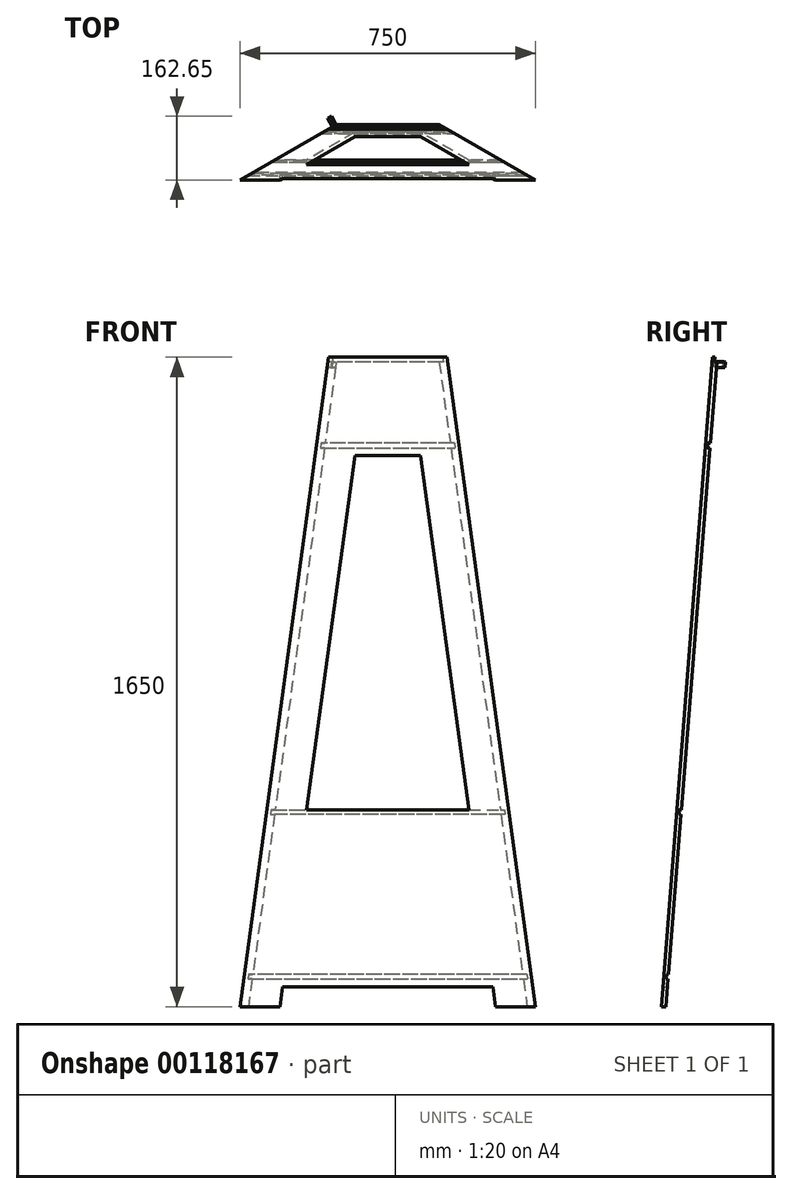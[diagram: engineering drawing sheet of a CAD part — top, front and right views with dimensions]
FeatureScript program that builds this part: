
annotation { "Feature Type Name" : "Feature", "Feature Type Description" : "" }
export const myFeature = defineFeature(function(context is Context, id is Id, definition is map)
    precondition{}
    {
        {
            var Q0;
            Q0=qCreatedBy(makeId("Front.planeOp"),FACE);
            var sketch = newSketch(context, id + "F0", { "sketchPlane" : qUnion([Q0])});
            skLineSegment(sketch, "E0", {"start": v(-375, 0) * mm, "end": v(375, 0) * mm});
            skLineSegment(sketch, "E1", {"start": v(0, 0) * mm, "end": v(0, 1650) * mm});
            skLineSegment(sketch, "E2", {"start": v(-150, 1650) * mm, "end": v(150, 1650) * mm});
            skSolve(sketch);
        }
        {
            var Q0;
            Q0=sQuery(id+"F0.wireOp",EDGE,"E2");
            cPoint(context, id + "F1", {"entities" : qUnion([Q0]), "parameter" : 0.5});
        }
        {
            var Q0;
            Q0 = qCreatedBy(id + "F1" ,VERTEX);
            var Q1;
            Q1=sQuery(id+"F0.wireOp",EDGE,"E1");
            cPlane(context, id + "F2", {"entities" : qUnion([Q0, Q1]), "cplaneType" : CPlaneType.LINE_POINT, "offset" : 25 * mm, "width" : 150 * mm, "height" : 150 * mm});
        }
        {
            var Q0;
            Q0=qCreatedBy(makeId("Top.planeOp"),FACE);
            var sketch = newSketch(context, id + "F3", { "sketchPlane" : qUnion([Q0])});
            skCircle(sketch, "E3.cCircle", {"center": v(0, 0) * mm, "radius": 216.5 * mm, "construction": true});
            skLineSegment(sketch, "E3.0", {"start": v(375, -216.5) * mm, "end": v(-375, -216.5) * mm});
            skLineSegment(sketch, "E3.1", {"start": v(-375, -216.5) * mm, "end": v(0, 433.01) * mm});
            skLineSegment(sketch, "E3.2", {"start": v(0, 433.01) * mm, "end": v(375, -216.5) * mm});
            skPoint(sketch, "E3.0.midPoint", {"position": v(0, -216.5) * mm});
            skSolve(sketch);
        }
        {
            var Q0;
            Q0=qCreatedBy(id+"F2.planeOp",FACE);
            var sketch = newSketch(context, id + "F4", { "sketchPlane" : qUnion([Q0])});
            skCircle(sketch, "E4.cCircle", {"center": v(0, 0) * mm, "radius": 86.6 * mm, "construction": true});
            skLineSegment(sketch, "E4.0", {"start": v(150, -86.6) * mm, "end": v(-150, -86.6) * mm});
            skLineSegment(sketch, "E4.1", {"start": v(-150, -86.6) * mm, "end": v(0, 173.2) * mm});
            skLineSegment(sketch, "E4.2", {"start": v(0, 173.2) * mm, "end": v(150, -86.6) * mm});
            skPoint(sketch, "E4.0.midPoint", {"position": v(0, -86.6) * mm});
            skSolve(sketch);
        }
        {
            var Q0;
            Q0=makeQuery(id+"F3.imprint","IMPRINT",FACE,{"disambiguationData":[TD([[makeQuery(id+"F3.imprint","IMPRINT",EDGE,{"derivedFrom":sQuery(id+"F3.wireOp",EDGE,"E3.0")}),-1.0]])]});
            var Q1;
            Q1=makeQuery(id+"F4.imprint","IMPRINT",FACE,{"disambiguationData":[TD([[makeQuery(id+"F4.imprint","IMPRINT",EDGE,{"derivedFrom":sQuery(id+"F4.wireOp",EDGE,"E4.0")}),-1.0]])]});
            loft(context, id + "F5", {"sheetProfilesArray" : [{ "sheetProfileEntities" : qUnion([Q0]) }, { "sheetProfileEntities" : qUnion([Q1]) }]});
        }
        {
            var Q0;
            {var subQ0=sQuery(id+"F4.wireOp",EDGE,"E4.0");var subQ1=sQuery(id+"F4.wireOp",EDGE,"E4.1");var subQ2=sQuery(id+"F4.wireOp",EDGE,"E4.2");var subQ3=sQuery(id+"F3.wireOp",EDGE,"E3.0");var subQ4=sQuery(id+"F3.wireOp",EDGE,"E3.1");var subQ5=sQuery(id+"F3.wireOp",EDGE,"E3.2");Q0=makeQuery(id+"F5.opLoft","SWEPT_FACE",FACE,{"disambiguationData":[OSD([subQ3,subQ4,subQ5,subQ0,subQ1,subQ2]),TDD([makeQuery(id+"F3.imprint","INTERSECT",VERTEX,{"derivedFrom":[subQ3,subQ5]}),makeQuery(id+"F3.imprint","INTERSECT",VERTEX,{"derivedFrom":[subQ3,subQ4]}),makeQuery(id+"F3.imprint","IMPRINT",EDGE,{"derivedFrom":subQ3}),makeQuery(id+"F4.imprint","INTERSECT",VERTEX,{"derivedFrom":[subQ0,subQ2]}),makeQuery(id+"F4.imprint","INTERSECT",VERTEX,{"derivedFrom":[subQ0,subQ1]}),makeQuery(id+"F4.imprint","IMPRINT",EDGE,{"derivedFrom":subQ0})])]});}
            cPlane(context, id + "F6", {"entities" : qUnion([Q0]), "cplaneType" : CPlaneType.OFFSET, "offset" : 12 * mm, "oppositeDirection" : true, "width" : 150 * mm, "height" : 150 * mm});
        }
        {
            var Q0;
            Q0=qCreatedBy(id+"F6.planeOp",FACE);
            var sketch = newSketch(context, id + "F7", { "sketchPlane" : qUnion([Q0])});
            skCircle(sketch, "E5", {"center": v(0, 812.97) * mm, "radius": 960.24 * mm});
            skSolve(sketch);
        }
        {
            var Q0;
            Q0 = qSketchRegion(id + "F7", true);
            extrude(context, id + "F8", {"entities" : qUnion([Q0]), "operationType" : NewBodyOperationType.REMOVE, "endBound" : BoundingType.THROUGH_ALL, "oppositeDirection" : true, "depth" : 25 * mm});
        }
        {
            var Q0;
            Q0=makeQuery(id+"F5.opLoft","CAP_FACE",FACE,{"disambiguationData":[OSD([makeQuery(id+"F4.imprint","IMPRINT",FACE,{"disambiguationData":[TD([[makeQuery(id+"F4.imprint","IMPRINT",EDGE,{"derivedFrom":sQuery(id+"F4.wireOp",EDGE,"E4.0")}),-1.0]])]})])],"isStart":true});
            var sketch = newSketch(context, id + "F9", { "sketchPlane" : qUnion([Q0])});
            skLineSegment(sketch, "E6", {"start": v(150, -86.6) * mm, "end": v(129.15, -74.57) * mm});
            skLineSegment(sketch, "E7", {"start": v(-150, -86.6) * mm, "end": v(-129.15, -74.57) * mm});
            skLineSegment(sketch, "E8", {"start": v(129.15, -74.57) * mm, "end": v(70, -40.41) * mm, "construction": true});
            skLineSegment(sketch, "E9", {"start": v(129.15, -74.57) * mm, "end": v(104.15, -31.26) * mm, "construction": true});
            skLineSegment(sketch, "E10", {"start": v(104.15, -31.26) * mm, "end": v(70, -40.41) * mm, "construction": true});
            skLineSegment(sketch, "E11.MirrorCS", {"start": v(79.15, -74.57) * mm, "end": v(70, -40.41) * mm, "construction": true});
            skLineSegment(sketch, "E12.MirrorCS", {"start": v(129.15, -74.57) * mm, "end": v(79.15, -74.57) * mm, "construction": true});
            skSolve(sketch);
        }
        {
            var Q0;
            Q0=makeQuery(id+"F5.opLoft","SWEPT_EDGE",EDGE,{"disambiguationData":[OSD([sQuery(id+"F3.wireOp",EDGE,"E3.0"),sQuery(id+"F3.wireOp",EDGE,"E3.1"),sQuery(id+"F4.wireOp",EDGE,"E4.0"),sQuery(id+"F4.wireOp",EDGE,"E4.1")])]});
            var Q1;
            Q1=sQuery(id+"F9.wireOp",EDGE,"E7");
            cPlane(context, id + "F10", {"entities" : qUnion([Q0, Q1]), "cplaneType" : CPlaneType.LINE_ANGLE, "offset" : 25 * mm, "angle" : 0 * degree, "width" : 150 * mm, "height" : 150 * mm});
        }
        {
            var Q0;
            Q0=makeQuery(id+"F5.opLoft","SWEPT_EDGE",EDGE,{"disambiguationData":[OSD([sQuery(id+"F3.wireOp",EDGE,"E3.0"),sQuery(id+"F3.wireOp",EDGE,"E3.2"),sQuery(id+"F4.wireOp",EDGE,"E4.0"),sQuery(id+"F4.wireOp",EDGE,"E4.2")])]});
            var Q1;
            Q1=sQuery(id+"F9.wireOp",EDGE,"E6");
            cPlane(context, id + "F11", {"entities" : qUnion([Q0, Q1]), "cplaneType" : CPlaneType.LINE_ANGLE, "offset" : 25 * mm, "angle" : 0 * degree, "width" : 150 * mm, "height" : 150 * mm});
        }
        {
            var Q0;
            Q0=qCreatedBy(id+"F11.planeOp",FACE);
            var sketch = newSketch(context, id + "F12", { "sketchPlane" : qUnion([Q0])});
            skCircle(sketch, "E13", {"center": v(304.07, 817.21) * mm, "radius": 870.23 * mm});
            skSolve(sketch);
        }
        {
            var Q0;
            Q0 = qSketchRegion(id + "F12", true);
            extrude(context, id + "F13", {"entities" : qUnion([Q0]), "operationType" : NewBodyOperationType.REMOVE, "oppositeDirection" : true, "depth" : 25 * mm});
        }
        {
            var Q0;
            Q0=qCreatedBy(id+"F10.planeOp",FACE);
            var sketch = newSketch(context, id + "F14", { "sketchPlane" : qUnion([Q0])});
            skCircle(sketch, "E14", {"center": v(291.65, 811.12) * mm, "radius": 892.94 * mm});
            skSolve(sketch);
        }
        {
            var Q0;
            Q0 = qSketchRegion(id + "F14", true);
            extrude(context, id + "F15", {"entities" : qUnion([Q0]), "operationType" : NewBodyOperationType.REMOVE, "depth" : 25 * mm});
        }
        {
            var Q0;
            Q0=qCreatedBy(makeId("Front.planeOp"),FACE);
            var sketch = newSketch(context, id + "F16", { "sketchPlane" : qUnion([Q0])});
            skLineSegment(sketch, "E15.0.0", {"start": v(-354.15, 0) * mm, "end": v(-129.15, 1650) * mm, "construction": true});
            skLineSegment(sketch, "E15.0.1", {"start": v(-129.15, 1650) * mm, "end": v(129.15, 1650) * mm});
            skLineSegment(sketch, "E15.0.2", {"start": v(129.15, 1650) * mm, "end": v(354.15, 0) * mm, "construction": true});
            skLineSegment(sketch, "E16.0.1", {"start": v(-150, 1650) * mm, "end": v(-375, 0) * mm, "construction": true});
            skLineSegment(sketch, "E16.0.3", {"start": v(375, 0) * mm, "end": v(150, 1650) * mm, "construction": true});
            skLineSegment(sketch, "E17", {"start": v(0, 0) * mm, "end": v(0, 50) * mm, "construction": true});
            skLineSegment(sketch, "E18", {"start": v(0, 1400) * mm, "end": v(0, 1650) * mm, "construction": true});
            skLineSegment(sketch, "E19", {"start": v(0, 1400) * mm, "end": v(0, 500) * mm, "construction": true});
            skLineSegment(sketch, "E20", {"start": v(0, 500) * mm, "end": v(0, 50) * mm, "construction": true});
            skLineSegment(sketch, "E21", {"start": v(205.9, 500) * mm, "end": v(-205.9, 500) * mm});
            skLineSegment(sketch, "E22", {"start": v(-205.9, 500) * mm, "end": v(-83.17, 1400) * mm});
            skLineSegment(sketch, "E23", {"start": v(-83.17, 1400) * mm, "end": v(83.17, 1400) * mm});
            skLineSegment(sketch, "E24", {"start": v(83.17, 1400) * mm, "end": v(205.9, 500) * mm});
            skLineSegment(sketch, "E25", {"start": v(-274.07, 0) * mm, "end": v(-267.26, 50) * mm});
            skLineSegment(sketch, "E26", {"start": v(-267.26, 50) * mm, "end": v(267.26, 50) * mm});
            skLineSegment(sketch, "E27", {"start": v(267.26, 50) * mm, "end": v(274.07, 0) * mm});
            skLineSegment(sketch, "E28", {"start": v(274.07, 0) * mm, "end": v(-274.07, 0) * mm});
            skSolve(sketch);
        }
        {
            var Q0;
            Q0=qCreatedBy(makeId("Front.planeOp"),FACE);
            var sketch = newSketch(context, id + "F17", { "sketchPlane" : qUnion([Q0])});
            skLineSegment(sketch, "E29.0", {"start": v(375, 0) * mm, "end": v(150, 1650) * mm, "construction": true});
            skLineSegment(sketch, "E30.0", {"start": v(129.15, 1650) * mm, "end": v(354.15, 0) * mm, "construction": true});
            skLineSegment(sketch, "E31.0", {"start": v(-354.15, 0) * mm, "end": v(-129.15, 1650) * mm, "construction": true});
            skLineSegment(sketch, "E32.0", {"start": v(-150, 1650) * mm, "end": v(-375, 0) * mm, "construction": true});
            skPoint(sketch, "E33.0", {"position": v(0, 50) * mm});
            skPoint(sketch, "E34.0", {"position": v(0, 500) * mm});
            skPoint(sketch, "E35.0", {"position": v(0, 1400) * mm});
            skLineSegment(sketch, "E36", {"start": v(181.36, 1420) * mm, "end": v(-181.36, 1420) * mm});
            skLineSegment(sketch, "E37", {"start": v(-181.36, 1420) * mm, "end": v(-179.73, 1432) * mm});
            skLineSegment(sketch, "E38", {"start": v(-179.73, 1432) * mm, "end": v(179.73, 1432) * mm});
            skLineSegment(sketch, "E39", {"start": v(181.36, 1420) * mm, "end": v(179.73, 1432) * mm});
            skLineSegment(sketch, "E40", {"start": v(150, 1650) * mm, "end": v(-150, 1650) * mm});
            skLineSegment(sketch, "E41", {"start": v(-150, 1650) * mm, "end": v(-151.64, 1638) * mm});
            skLineSegment(sketch, "E42", {"start": v(-151.64, 1638) * mm, "end": v(151.64, 1638) * mm});
            skLineSegment(sketch, "E43", {"start": v(306.82, 500) * mm, "end": v(-306.82, 500) * mm});
            skLineSegment(sketch, "E44", {"start": v(-306.82, 500) * mm, "end": v(-308.45, 488) * mm});
            skLineSegment(sketch, "E45", {"start": v(-308.45, 488) * mm, "end": v(308.45, 488) * mm});
            skLineSegment(sketch, "E46", {"start": v(306.82, 500) * mm, "end": v(308.45, 488) * mm});
            skLineSegment(sketch, "E47", {"start": v(365.45, 70) * mm, "end": v(-365.45, 70) * mm});
            skLineSegment(sketch, "E48", {"start": v(-365.45, 70) * mm, "end": v(-363.82, 82) * mm});
            skLineSegment(sketch, "E49", {"start": v(-363.82, 82) * mm, "end": v(363.82, 82) * mm});
            skLineSegment(sketch, "E50", {"start": v(363.82, 82) * mm, "end": v(365.45, 70) * mm});
            skLineSegment(sketch, "E51", {"start": v(150, 1650) * mm, "end": v(151.64, 1638) * mm});
            skSolve(sketch);
        }
        {
            var Q0;
            Q0=makeQuery(id+"F8.boolean.opBoolean","COPY",FACE,{"derivedFrom":makeQuery(id+"F8.opExtrude","CAP_FACE",FACE,{"disambiguationData":[OSD([sQuery(id+"F7.wireOp",EDGE,"E5")])],"isStart":true})});
            cPlane(context, id + "F18", {"entities" : qUnion([Q0]), "cplaneType" : CPlaneType.OFFSET, "offset" : 6 * mm, "oppositeDirection" : true, "width" : 150 * mm, "height" : 150 * mm});
        }
        {
            var Q0;
            Q0 = qSketchRegion(id + "F17", true);
            var Q1;
            Q1=qCreatedBy(id+"F18.planeOp",FACE);
            extrude(context, id + "F19", {"entities" : qUnion([Q0]), "operationType" : NewBodyOperationType.REMOVE, "endBound" : BoundingType.UP_TO_SURFACE, "endBoundEntityFace" : qUnion([Q1]), "depth" : 25 * mm});
        }
        {
            var Q0;
            Q0=makeQuery(id+"F16.imprint","IMPRINT",FACE,{"disambiguationData":[TD([[makeQuery(id+"F16.imprint","IMPRINT",EDGE,{"derivedFrom":sQuery(id+"F16.wireOp",EDGE,"E25")}),-1.0]])]});
            var Q1;
            Q1=makeQuery(id+"F16.imprint","IMPRINT",FACE,{"disambiguationData":[TD([[makeQuery(id+"F16.imprint","IMPRINT",EDGE,{"derivedFrom":sQuery(id+"F16.wireOp",EDGE,"E21")}),-1.0]])]});
            extrude(context, id + "F20", {"entities" : qUnion([Q0, Q1]), "operationType" : NewBodyOperationType.REMOVE, "endBound" : BoundingType.THROUGH_ALL, "depth" : 25 * mm});
        }
        {
            var Q0;
            Q0=makeQuery(id+"F19.boolean.opBoolean","INTERSECT",EDGE,{"derivedFrom":[makeQuery(id+"F15.boolean.opBoolean","COPY",FACE,{"derivedFrom":makeQuery(id+"F15.opExtrude","CAP_FACE",FACE,{"disambiguationData":[OSD([sQuery(id+"F14.wireOp",EDGE,"E14")])],"isStart":true})}),makeQuery(id+"F19.opExtrude","SWEPT_FACE",FACE,{"disambiguationData":[OSD([sQuery(id+"F17.wireOp",EDGE,"E42")])]})]});
            var Q1;
            {var subQ0=makeQuery(id+"F8.boolean.opBoolean","COPY",FACE,{"derivedFrom":makeQuery(id+"F8.opExtrude","CAP_FACE",FACE,{"disambiguationData":[OSD([sQuery(id+"F7.wireOp",EDGE,"E5")])],"isStart":true})});var subQ1=makeQuery(id+"F15.opExtrude","CAP_FACE",FACE,{"disambiguationData":[OSD([sQuery(id+"F14.wireOp",EDGE,"E14")])],"isStart":true});Q1=makeQuery(id+"F19.boolean.opBoolean","SPLIT",EDGE,{"disambiguationData":[TD([makeQuery(id+"F19.opExtrude","SWEPT_FACE",FACE,{"disambiguationData":[OSD([sQuery(id+"F17.wireOp",EDGE,"E38")])]})])],"derivedFrom":makeQuery(id+"F15.boolean.opBoolean","INTERSECT",EDGE,{"derivedFrom":[subQ0,subQ1]})});}
            cPlane(context, id + "F21", {"entities" : qUnion([Q0, Q1]), "cplaneType" : CPlaneType.LINE_ANGLE, "offset" : 25 * mm, "angle" : 0 * degree, "width" : 150 * mm, "height" : 150 * mm});
        }
        {
            var Q0;
            Q0=qCreatedBy(id+"F21.planeOp",FACE);
            var sketch = newSketch(context, id + "F22", { "sketchPlane" : qUnion([Q0])});
            skLineSegment(sketch, "E52", {"start": v(151.02, 1638) * mm, "end": v(153.22, 1624.02) * mm});
            skLineSegment(sketch, "E53", {"start": v(153.22, 1624.02) * mm, "end": v(162.42, 1625.47) * mm});
            skLineSegment(sketch, "E54", {"start": v(162.42, 1625.47) * mm, "end": v(160.22, 1639.45) * mm});
            skLineSegment(sketch, "E55", {"start": v(160.22, 1639.45) * mm, "end": v(151.02, 1638) * mm});
            skSolve(sketch);
        }
        {
            var Q0;
            Q0 = qSketchRegion(id + "F22", true);
            extrude(context, id + "F23", {"entities" : qUnion([Q0]), "operationType" : NewBodyOperationType.ADD, "depth" : 25 * mm});
        }
        {
            var Q0;
            Q0=makeQuery(id+"F23.opExtrude","SWEPT_FACE",FACE,{"disambiguationData":[OSD([sQuery(id+"F22.wireOp",EDGE,"E55")])]});
            cPlane(context, id + "F24", {"entities" : qUnion([Q0]), "cplaneType" : CPlaneType.OFFSET, "offset" : 0 * mm, "width" : 150 * mm, "height" : 150 * mm});
        }
    });
